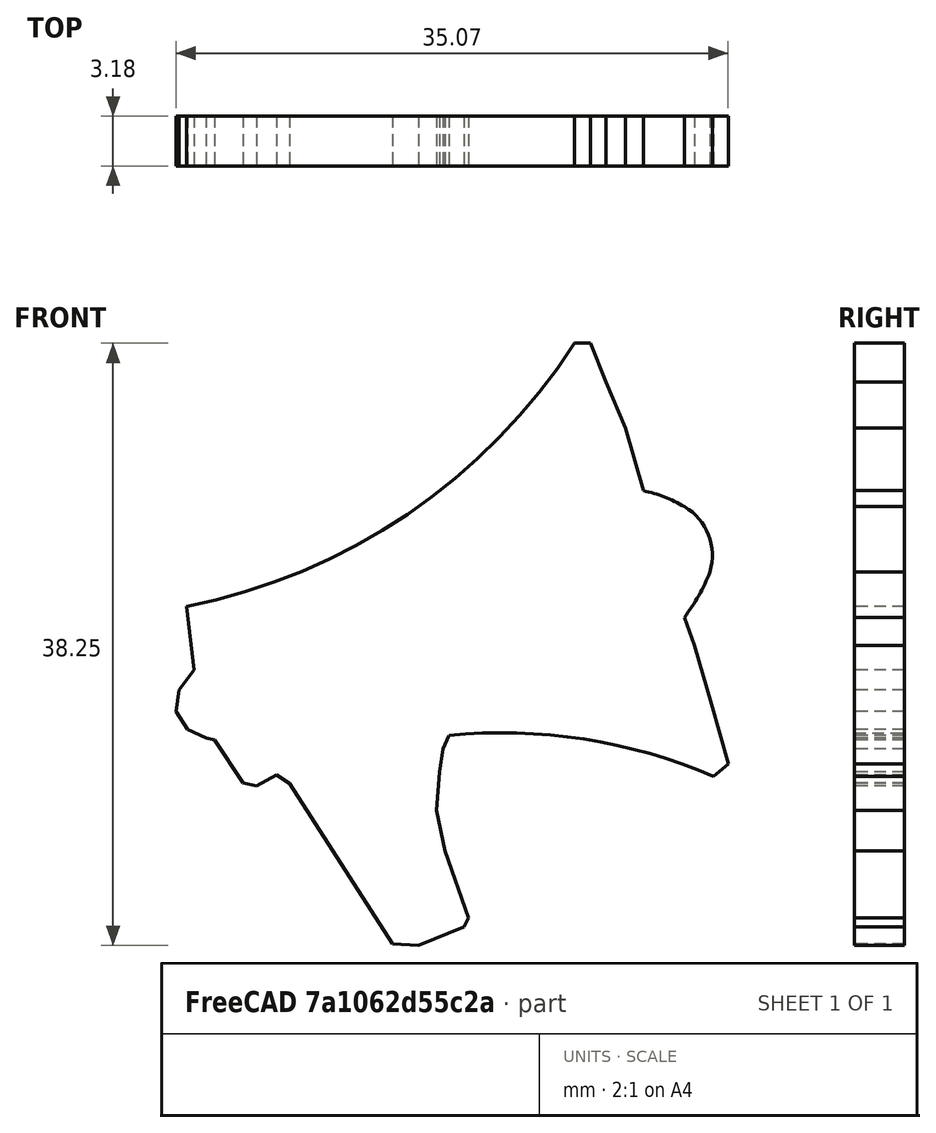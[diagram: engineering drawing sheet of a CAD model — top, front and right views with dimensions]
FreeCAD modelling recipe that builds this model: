
FCSTD DOCUMENT  (FreeCAD 0.20R27809 (Git))
Label: Outreach_Template
License: All rights reserved
LicenseURL: http://en.wikipedia.org/wiki/All_rights_reserved
objects: Image::ImagePlane×1, Sketcher::SketchObject×1, PartDesign::Pad×1, PartDesign::Body×1
note: 4 computed .brp shape members not serialized (recipe doc carries the construction recipe); baked Part::Feature solids carry a one-line shape summary decoded from their .brp

FEATURE [Image::ImagePlane] ImagePlane
  Placement = pos=(0,0,0) rot=(-1,0,0;4.71239rad)
  XSize = 39.37
  YSize = 39.37
FEATURE [Sketcher::SketchObject] Sketch
  FullyConstrained = false
  MapMode = 5
  Placement = pos=(0,0,0) rot=(1,0,0;1.5708rad)
  Support = -> [XZ_Plane]
  sketch-geometry (32):
    g0: ArcOfCircle CenterX=-24.2946 CenterY=39.7087 CenterZ=0 NormalX=0 NormalY=0 NormalZ=1 AngleXU=0 Radius=37.926 StartAngle=4.90545 EndAngle=5.71191
    g1: LineSegment StartX=-17.018 StartY=2.48733 StartZ=0 EndX=-16.5501 EndY=-1.56106 EndZ=0
    g2: LineSegment StartX=-16.5501 StartY=-1.56106 StartZ=0 EndX=-17.5029 EndY=-2.81874 EndZ=0
    g3: LineSegment StartX=-17.5029 StartY=-2.81874 StartZ=0 EndX=-17.6934 EndY=-4.19076 EndZ=0
    g4: LineSegment StartX=-17.6934 StartY=-4.19076 StartZ=0 EndX=-16.9693 EndY=-5.33411 EndZ=0
    g5: LineSegment StartX=-16.9693 StartY=-5.33411 StartZ=0 EndX=-15.7879 EndY=-5.86767 EndZ=0
    g6: LineSegment StartX=-15.7879 StartY=-5.86767 StartZ=0 EndX=-15.2543 EndY=-5.98201 EndZ=0
    g7: LineSegment StartX=-15.2543 StartY=-5.98201 StartZ=0 EndX=-13.4249 EndY=-8.72605 EndZ=0
    g8: LineSegment StartX=-13.4249 StartY=-8.72605 StartZ=0 EndX=-12.5865 EndY=-8.9166 EndZ=0
    g9: LineSegment StartX=-12.5865 StartY=-8.9166 StartZ=0 EndX=-11.2907 EndY=-8.23059 EndZ=0
    g10: LineSegment StartX=-11.2907 StartY=-8.23059 StartZ=0 EndX=-10.4903 EndY=-8.76416 EndZ=0
    g11: LineSegment StartX=-10.4903 StartY=-8.76416 StartZ=0 EndX=-3.95384 EndY=-18.9441 EndZ=0
    g12: LineSegment StartX=-3.95384 StartY=-18.9441 StartZ=0 EndX=-2.27488 EndY=-19.0508 EndZ=0
    g13: LineSegment StartX=-2.27488 StartY=-19.0508 StartZ=0 EndX=0.602916 EndY=-17.8614 EndZ=0
    g14: LineSegment StartX=0.602916 StartY=-17.8614 StartZ=0 EndX=0.885784 EndY=-17.3032 EndZ=0
    g15: LineSegment StartX=0.885784 StartY=-17.3032 StartZ=0 EndX=-0.608809 EndY=-13.056 EndZ=0
    g16: LineSegment StartX=-0.608809 StartY=-13.056 StartZ=0 EndX=-1.15232 EndY=-10.4654 EndZ=0
    g17: LineSegment StartX=-1.15232 StartY=-10.4654 StartZ=0 EndX=-0.958348 EndY=-8.02406 EndZ=0
    g18: LineSegment StartX=-0.958348 StartY=-8.02406 StartZ=0 EndX=-0.734469 EndY=-6.57729 EndZ=0
    g19: LineSegment StartX=-0.734469 StartY=-6.57729 StartZ=0 EndX=-0.364355 EndY=-5.70101 EndZ=0
    g20: LineSegment StartX=16.4535 StartY=-8.3103 StartZ=0 EndX=17.3813 EndY=-7.53316 EndZ=0
    g21: LineSegment StartX=17.3813 StartY=-7.53316 StartZ=0 EndX=16.3107 EndY=-3.71609 EndZ=0
    g22: LineSegment StartX=16.3107 StartY=-3.71609 StartZ=0 EndX=15.2401 EndY=0.007885 EndZ=0
    g23: LineSegment StartX=15.2401 StartY=0.007885 StartZ=0 EndX=14.5915 EndY=1.79097 EndZ=0
    g24: LineSegment StartX=7.60914 StartY=19.2018 StartZ=0 EndX=8.63315 EndY=19.2018 EndZ=0
    g25: LineSegment StartX=8.63315 StartY=19.2018 StartZ=0 EndX=9.61069 EndY=16.7334 EndZ=0
    g26: LineSegment StartX=9.61069 StartY=16.7334 StartZ=0 EndX=10.8675 EndY=13.8008 EndZ=0
    g27: LineSegment StartX=10.8675 StartY=13.8008 StartZ=0 EndX=11.9912 EndY=9.83463 EndZ=0
    g28: ArcOfCircle CenterX=2.95991 CenterY=-39.7781 CenterZ=0 NormalX=0 NormalY=0 NormalZ=1 AngleXU=0 Radius=34.2389 StartAngle=1.16571 EndAngle=1.66804
    g29: ArcOfCircle CenterX=10.3001 CenterY=1.66151 CenterZ=0 NormalX=0 NormalY=0 NormalZ=1 AngleXU=0 Radius=8.34622 StartAngle=1.03076 EndAngle=1.36678
    g30: ArcOfCircle CenterX=12.8117 CenterY=5.72818 CenterZ=0 NormalX=0 NormalY=0 NormalZ=1 AngleXU=0 Radius=3.56746 StartAngle=5.98409 EndAngle=7.33167
    g31: ArcOfCircle CenterX=5.67216 CenterY=8.72936 CenterZ=0 NormalX=0 NormalY=0 NormalZ=1 AngleXU=0 Radius=11.3003 StartAngle=5.62206 EndAngle=5.91641
  constraints (49):
    c: DistanceX(g0) = 7.60914
    c: DistanceY(g0) = 19.2018
    c: DistanceX(g0) = -17.018
    c: DistanceY(g0) = 2.48733
    c: Coincident(g1,g0)
    c: Coincident(g2,g1)
    c: Coincident(g2,g3)
    c: Coincident(g3,g4)
    c: Coincident(g4,g5)
    c: Coincident(g5,g6)
    c: Coincident(g6,g7)
    c: Coincident(g7,g8)
    c: Coincident(g8,g9)
    c: Coincident(g9,g10)
    c: Coincident(g10,g11)
    c: Coincident(g11,g12)
    c: Coincident(g12,g13)
    c: Coincident(g13,g14)
    c: Coincident(g14,g15)
    c: Coincident(g15,g16)
    c: Coincident(g16,g17)
    c: Coincident(g17,g18)
    c: Coincident(g18,g19)
    c: Coincident(g20,g21)
    c: Coincident(g21,g22)
    c: Coincident(g22,g23)
    c: Coincident(g24,g0)
    c: Horizontal(g24)
    c: Coincident(g25,g24)
    c: Coincident(g26,g25)
    c: Coincident(g27,g26)
    c: Coincident(g28,g19)
    c: DistanceX(g19) = -0.364355
    c: DistanceY(g19) = -5.70101
    c: Coincident(g28,g20)
    c: DistanceX(g20) = 16.4535
    c: DistanceY(g20) = -8.3103
    c: Coincident(g29,g27)
    c: Coincident(g30,g29)
    c: Coincident(g31,g30)
    c: Coincident(g31,g23)
    c: DistanceX(g23) = 14.5915
    c: DistanceY(g23) = 1.79097
    c: DistanceX(g27) = 11.9912
    c: DistanceY(g27) = 9.83463
    c: DistanceX(g29) = 14.5915
    c: DistanceY(g29) = 8.81998
    c: DistanceX(g30) = 16.2208
    c: DistanceY(g30) = 4.67701
FEATURE [PartDesign::Pad] Pad
  Direction = (0,-1,-2e-16)
  Length = 3.175
  Length2 = 10.0076
  Placement = pos=(0,0,0) rot=(1,0,0;1.5708rad)
  Profile = -> Sketch
  ReferenceAxis = -> Sketch [N_Axis]
  Type = 0
FEATURE [PartDesign::Body] Body  label="Outreach Body"
  Group = -> [Sketch,Pad]
  Origin = -> Origin
  Tip = -> Pad
